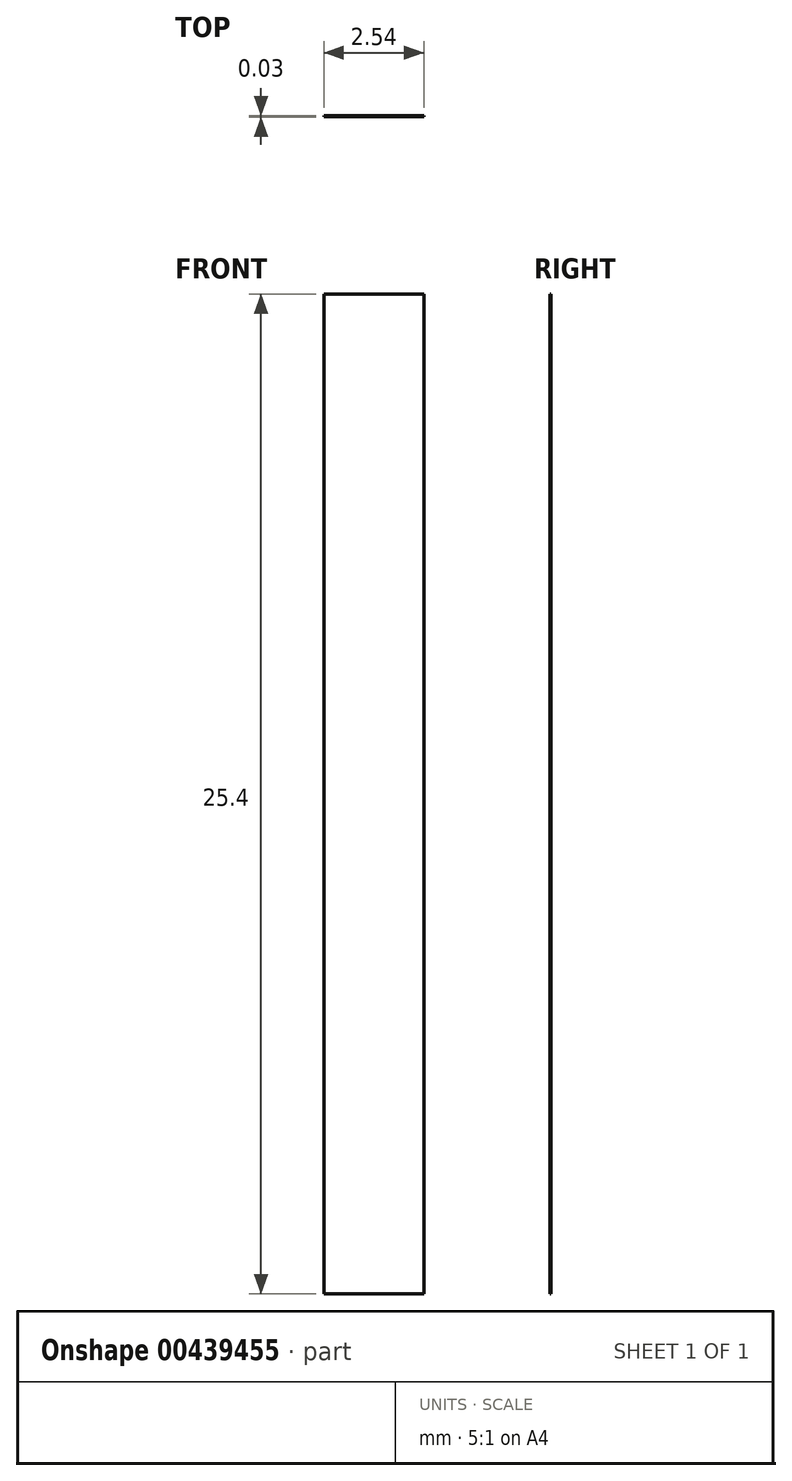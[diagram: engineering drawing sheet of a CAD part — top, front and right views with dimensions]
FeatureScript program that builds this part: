
annotation { "Feature Type Name" : "Feature", "Feature Type Description" : "" }
export const myFeature = defineFeature(function(context is Context, id is Id, definition is map)
    precondition{}
    {
        {
            var Q0;
            Q0=qCreatedBy(makeId("Front.planeOp"),FACE);
            var sketch = newSketch(context, id + "F0", { "sketchPlane" : qUnion([Q0])});
            skLineSegment(sketch, "E0.bottom", {"start": v(0, 25.4) * mm, "end": v(-2.54, 25.4) * mm});
            skLineSegment(sketch, "E0.top", {"start": v(0, 0) * mm, "end": v(-2.54, 0) * mm});
            skLineSegment(sketch, "E0.left", {"start": v(0, 25.4) * mm, "end": v(0, 0) * mm});
            skLineSegment(sketch, "E0.right", {"start": v(-2.54, 25.4) * mm, "end": v(-2.54, 0) * mm});
            skSolve(sketch);
        }
        {
            var Q0;
            Q0=makeQuery(id+"F0.imprint","IMPRINT",FACE,{"disambiguationData":[TD([[makeQuery(id+"F0.imprint","IMPRINT",EDGE,{"derivedFrom":sQuery(id+"F0.wireOp",EDGE,"E0.bottom")}),1.0]])]});
            extrude(context, id + "F1", {"entities" : qUnion([Q0]), "depth" : 0.03 * mm});
        }
    });
